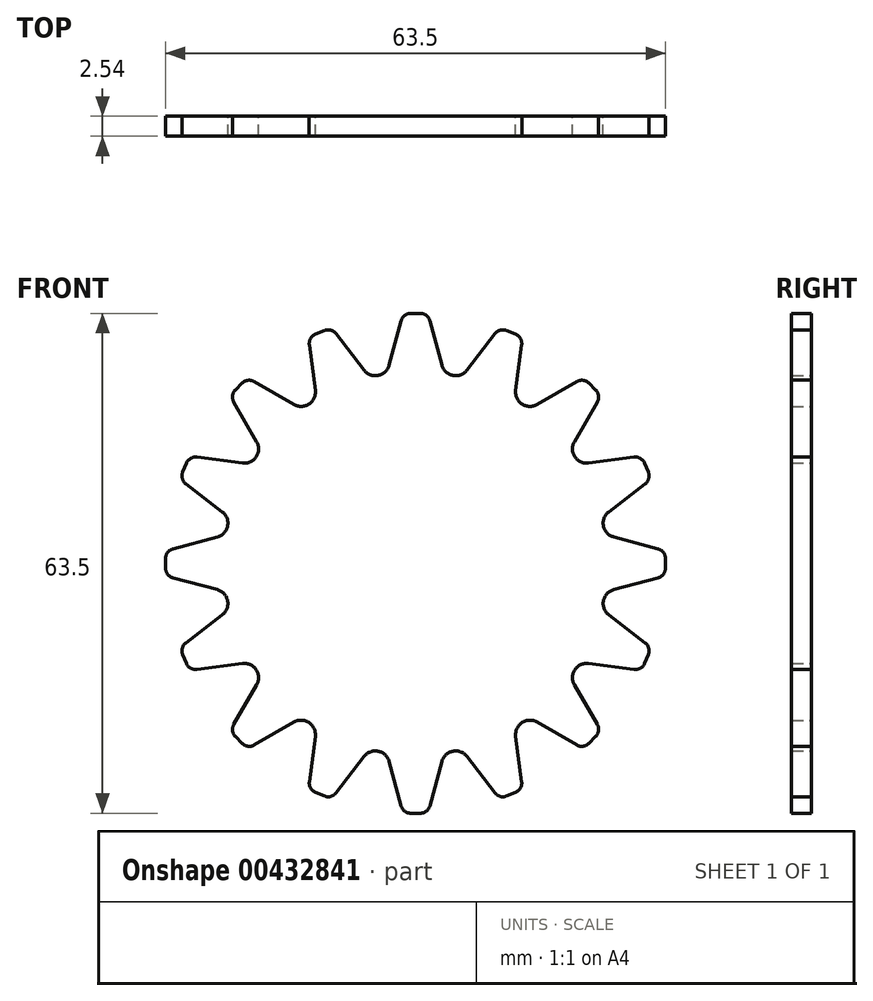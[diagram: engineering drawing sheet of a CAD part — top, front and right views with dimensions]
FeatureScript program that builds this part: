
annotation { "Feature Type Name" : "Feature", "Feature Type Description" : "" }
export const myFeature = defineFeature(function(context is Context, id is Id, definition is map)
    precondition{}
    {
        {
            var Q0;
            Q0=qCreatedBy(makeId("Front.planeOp"),FACE);
            var sketch = newSketch(context, id + "F0", { "sketchPlane" : qUnion([Q0])});
            skCircle(sketch, "E0", {"center": v(0, 0) * mm, "radius": 25.4 * mm, "construction": true});
            skLineSegment(sketch, "E1", {"start": v(0, 48.3) * mm, "end": v(0, -16.63) * mm, "construction": true});
            skPoint(sketch, "E2", {"position": v(0, 31.75) * mm});
            skLineSegment(sketch, "E3", {"start": v(1.59, 31.75) * mm, "end": v(-0.61, 31.75) * mm});
            skLineSegment(sketch, "E4", {"start": v(-1.84, 30.8) * mm, "end": v(-3.35, 25.18) * mm});
            skPoint(sketch, "E5.visualSharp", {"position": v(-1.59, 31.75) * mm});
            skArc(sketch, "E5.filletArc", {"start": v(-0.61, 31.75) * mm, "mid": v(-1.39, 31.49) * mm, "end": v(-1.84, 30.8) * mm});
            skLineSegment(sketch, "E6.MirrorCS", {"start": v(1.84, 30.8) * mm, "end": v(3.35, 25.18) * mm});
            skArc(sketch, "E7.MirrorCS", {"start": v(0.61, 31.75) * mm, "mid": v(1.39, 31.49) * mm, "end": v(1.84, 30.8) * mm});
            skArc(sketch, "E8", {"start": v(3.35, 25.18) * mm, "mid": v(4.75, 23.87) * mm, "end": v(6.54, 24.54) * mm});
            skLineSegment(sketch, "E9.1.0", {"start": v(-10.1, 29.17) * mm, "end": v(-6.54, 24.54) * mm});
            skPoint(sketch, "E9.1.1", {"position": v(-13.62, 28.73) * mm});
            skLineSegment(sketch, "E9.1.2", {"start": v(-13.49, 27.76) * mm, "end": v(-12.73, 21.98) * mm});
            skArc(sketch, "E9.1.3", {"start": v(-6.54, 24.54) * mm, "mid": v(-4.75, 23.87) * mm, "end": v(-3.35, 25.18) * mm});
            skPoint(sketch, "E9.1.4", {"position": v(-12.15, 29.33) * mm});
            skLineSegment(sketch, "E9.1.5", {"start": v(-10.68, 29.94) * mm, "end": v(-12.72, 29.1) * mm});
            skArc(sketch, "E9.1.6", {"start": v(-11.58, 29.57) * mm, "mid": v(-10.77, 29.62) * mm, "end": v(-10.1, 29.17) * mm});
            skArc(sketch, "E9.1.7", {"start": v(-12.72, 29.1) * mm, "mid": v(-13.33, 28.56) * mm, "end": v(-13.49, 27.76) * mm});
            skLineSegment(sketch, "E9.2.0", {"start": v(-20.48, 23.09) * mm, "end": v(-15.44, 20.17) * mm});
            skPoint(sketch, "E9.2.1", {"position": v(-23.57, 21.33) * mm});
            skLineSegment(sketch, "E9.2.2", {"start": v(-23.09, 20.48) * mm, "end": v(-20.17, 15.44) * mm});
            skArc(sketch, "E9.2.3", {"start": v(-15.44, 20.17) * mm, "mid": v(-13.52, 20.23) * mm, "end": v(-12.73, 21.98) * mm});
            skPoint(sketch, "E9.2.4", {"position": v(-22.45, 22.45) * mm});
            skLineSegment(sketch, "E9.2.5", {"start": v(-21.33, 23.57) * mm, "end": v(-22.88, 22.02) * mm});
            skArc(sketch, "E9.2.6", {"start": v(-22.02, 22.88) * mm, "mid": v(-21.28, 23.25) * mm, "end": v(-20.48, 23.09) * mm});
            skArc(sketch, "E9.2.7", {"start": v(-22.88, 22.02) * mm, "mid": v(-23.25, 21.28) * mm, "end": v(-23.09, 20.48) * mm});
            skLineSegment(sketch, "E9.3.0", {"start": v(-27.76, 13.49) * mm, "end": v(-21.98, 12.73) * mm});
            skPoint(sketch, "E9.3.1", {"position": v(-29.94, 10.68) * mm});
            skLineSegment(sketch, "E9.3.2", {"start": v(-29.17, 10.1) * mm, "end": v(-24.54, 6.54) * mm});
            skArc(sketch, "E9.3.3", {"start": v(-21.98, 12.73) * mm, "mid": v(-20.23, 13.52) * mm, "end": v(-20.17, 15.44) * mm});
            skPoint(sketch, "E9.3.4", {"position": v(-29.33, 12.15) * mm});
            skLineSegment(sketch, "E9.3.5", {"start": v(-28.73, 13.62) * mm, "end": v(-29.57, 11.58) * mm});
            skArc(sketch, "E9.3.6", {"start": v(-29.1, 12.72) * mm, "mid": v(-28.56, 13.33) * mm, "end": v(-27.76, 13.49) * mm});
            skArc(sketch, "E9.3.7", {"start": v(-29.57, 11.58) * mm, "mid": v(-29.62, 10.77) * mm, "end": v(-29.17, 10.1) * mm});
            skLineSegment(sketch, "E9.4.0", {"start": v(-30.8, 1.84) * mm, "end": v(-25.18, 3.35) * mm});
            skPoint(sketch, "E9.4.1", {"position": v(-31.75, -1.59) * mm});
            skLineSegment(sketch, "E9.4.2", {"start": v(-30.8, -1.84) * mm, "end": v(-25.18, -3.35) * mm});
            skArc(sketch, "E9.4.3", {"start": v(-25.18, 3.35) * mm, "mid": v(-23.87, 4.75) * mm, "end": v(-24.54, 6.54) * mm});
            skPoint(sketch, "E9.4.4", {"position": v(-31.75, 0) * mm});
            skLineSegment(sketch, "E9.4.5", {"start": v(-31.75, 1.59) * mm, "end": v(-31.75, -0.61) * mm});
            skArc(sketch, "E9.4.6", {"start": v(-31.75, 0.61) * mm, "mid": v(-31.49, 1.39) * mm, "end": v(-30.8, 1.84) * mm});
            skArc(sketch, "E9.4.7", {"start": v(-31.75, -0.61) * mm, "mid": v(-31.49, -1.39) * mm, "end": v(-30.8, -1.84) * mm});
            skLineSegment(sketch, "E9.5.0", {"start": v(-29.17, -10.1) * mm, "end": v(-24.54, -6.54) * mm});
            skPoint(sketch, "E9.5.1", {"position": v(-28.73, -13.62) * mm});
            skLineSegment(sketch, "E9.5.2", {"start": v(-27.76, -13.49) * mm, "end": v(-21.98, -12.73) * mm});
            skArc(sketch, "E9.5.3", {"start": v(-24.54, -6.54) * mm, "mid": v(-23.87, -4.75) * mm, "end": v(-25.18, -3.35) * mm});
            skPoint(sketch, "E9.5.4", {"position": v(-29.33, -12.15) * mm});
            skLineSegment(sketch, "E9.5.5", {"start": v(-29.94, -10.68) * mm, "end": v(-29.1, -12.72) * mm});
            skArc(sketch, "E9.5.6", {"start": v(-29.57, -11.58) * mm, "mid": v(-29.62, -10.77) * mm, "end": v(-29.17, -10.1) * mm});
            skArc(sketch, "E9.5.7", {"start": v(-29.1, -12.72) * mm, "mid": v(-28.56, -13.33) * mm, "end": v(-27.76, -13.49) * mm});
            skLineSegment(sketch, "E9.6.0", {"start": v(-23.09, -20.48) * mm, "end": v(-20.17, -15.44) * mm});
            skPoint(sketch, "E9.6.1", {"position": v(-21.33, -23.57) * mm});
            skLineSegment(sketch, "E9.6.2", {"start": v(-20.48, -23.09) * mm, "end": v(-15.44, -20.17) * mm});
            skArc(sketch, "E9.6.3", {"start": v(-20.17, -15.44) * mm, "mid": v(-20.23, -13.52) * mm, "end": v(-21.98, -12.73) * mm});
            skPoint(sketch, "E9.6.4", {"position": v(-22.45, -22.45) * mm});
            skLineSegment(sketch, "E9.6.5", {"start": v(-23.57, -21.33) * mm, "end": v(-22.02, -22.88) * mm});
            skArc(sketch, "E9.6.6", {"start": v(-22.88, -22.02) * mm, "mid": v(-23.25, -21.28) * mm, "end": v(-23.09, -20.48) * mm});
            skArc(sketch, "E9.6.7", {"start": v(-22.02, -22.88) * mm, "mid": v(-21.28, -23.25) * mm, "end": v(-20.48, -23.09) * mm});
            skLineSegment(sketch, "E9.7.0", {"start": v(-13.49, -27.76) * mm, "end": v(-12.73, -21.98) * mm});
            skPoint(sketch, "E9.7.1", {"position": v(-10.68, -29.94) * mm});
            skLineSegment(sketch, "E9.7.2", {"start": v(-10.1, -29.17) * mm, "end": v(-6.54, -24.54) * mm});
            skArc(sketch, "E9.7.3", {"start": v(-12.73, -21.98) * mm, "mid": v(-13.52, -20.23) * mm, "end": v(-15.44, -20.17) * mm});
            skPoint(sketch, "E9.7.4", {"position": v(-12.15, -29.33) * mm});
            skLineSegment(sketch, "E9.7.5", {"start": v(-13.62, -28.73) * mm, "end": v(-11.58, -29.57) * mm});
            skArc(sketch, "E9.7.6", {"start": v(-12.72, -29.1) * mm, "mid": v(-13.33, -28.56) * mm, "end": v(-13.49, -27.76) * mm});
            skArc(sketch, "E9.7.7", {"start": v(-11.58, -29.57) * mm, "mid": v(-10.77, -29.62) * mm, "end": v(-10.1, -29.17) * mm});
            skLineSegment(sketch, "E9.8.0", {"start": v(-1.84, -30.8) * mm, "end": v(-3.35, -25.18) * mm});
            skPoint(sketch, "E9.8.1", {"position": v(1.59, -31.75) * mm});
            skLineSegment(sketch, "E9.8.2", {"start": v(1.84, -30.8) * mm, "end": v(3.35, -25.18) * mm});
            skArc(sketch, "E9.8.3", {"start": v(-3.35, -25.18) * mm, "mid": v(-4.75, -23.87) * mm, "end": v(-6.54, -24.54) * mm});
            skPoint(sketch, "E9.8.4", {"position": v(0, -31.75) * mm});
            skLineSegment(sketch, "E9.8.5", {"start": v(-1.59, -31.75) * mm, "end": v(0.61, -31.75) * mm});
            skArc(sketch, "E9.8.6", {"start": v(-0.61, -31.75) * mm, "mid": v(-1.39, -31.49) * mm, "end": v(-1.84, -30.8) * mm});
            skArc(sketch, "E9.8.7", {"start": v(0.61, -31.75) * mm, "mid": v(1.39, -31.49) * mm, "end": v(1.84, -30.8) * mm});
            skLineSegment(sketch, "E9.9.0", {"start": v(10.1, -29.17) * mm, "end": v(6.54, -24.54) * mm});
            skPoint(sketch, "E9.9.1", {"position": v(13.62, -28.73) * mm});
            skLineSegment(sketch, "E9.9.2", {"start": v(13.49, -27.76) * mm, "end": v(12.73, -21.98) * mm});
            skArc(sketch, "E9.9.3", {"start": v(6.54, -24.54) * mm, "mid": v(4.75, -23.87) * mm, "end": v(3.35, -25.18) * mm});
            skPoint(sketch, "E9.9.4", {"position": v(12.15, -29.33) * mm});
            skLineSegment(sketch, "E9.9.5", {"start": v(10.68, -29.94) * mm, "end": v(12.72, -29.1) * mm});
            skArc(sketch, "E9.9.6", {"start": v(11.58, -29.57) * mm, "mid": v(10.77, -29.62) * mm, "end": v(10.1, -29.17) * mm});
            skArc(sketch, "E9.9.7", {"start": v(12.72, -29.1) * mm, "mid": v(13.33, -28.56) * mm, "end": v(13.49, -27.76) * mm});
            skLineSegment(sketch, "E9.10.0", {"start": v(20.48, -23.09) * mm, "end": v(15.44, -20.17) * mm});
            skPoint(sketch, "E9.10.1", {"position": v(23.57, -21.33) * mm});
            skLineSegment(sketch, "E9.10.2", {"start": v(23.09, -20.48) * mm, "end": v(20.17, -15.44) * mm});
            skArc(sketch, "E9.10.3", {"start": v(15.44, -20.17) * mm, "mid": v(13.52, -20.23) * mm, "end": v(12.73, -21.98) * mm});
            skPoint(sketch, "E9.10.4", {"position": v(22.45, -22.45) * mm});
            skLineSegment(sketch, "E9.10.5", {"start": v(21.33, -23.57) * mm, "end": v(22.88, -22.02) * mm});
            skArc(sketch, "E9.10.6", {"start": v(22.02, -22.88) * mm, "mid": v(21.28, -23.25) * mm, "end": v(20.48, -23.09) * mm});
            skArc(sketch, "E9.10.7", {"start": v(22.88, -22.02) * mm, "mid": v(23.25, -21.28) * mm, "end": v(23.09, -20.48) * mm});
            skLineSegment(sketch, "E9.11.0", {"start": v(27.76, -13.49) * mm, "end": v(21.98, -12.73) * mm});
            skPoint(sketch, "E9.11.1", {"position": v(29.94, -10.68) * mm});
            skLineSegment(sketch, "E9.11.2", {"start": v(29.17, -10.1) * mm, "end": v(24.54, -6.54) * mm});
            skArc(sketch, "E9.11.3", {"start": v(21.98, -12.73) * mm, "mid": v(20.23, -13.52) * mm, "end": v(20.17, -15.44) * mm});
            skPoint(sketch, "E9.11.4", {"position": v(29.33, -12.15) * mm});
            skLineSegment(sketch, "E9.11.5", {"start": v(28.73, -13.62) * mm, "end": v(29.57, -11.58) * mm});
            skArc(sketch, "E9.11.6", {"start": v(29.1, -12.72) * mm, "mid": v(28.56, -13.33) * mm, "end": v(27.76, -13.49) * mm});
            skArc(sketch, "E9.11.7", {"start": v(29.57, -11.58) * mm, "mid": v(29.62, -10.77) * mm, "end": v(29.17, -10.1) * mm});
            skLineSegment(sketch, "E9.12.0", {"start": v(30.8, -1.84) * mm, "end": v(25.18, -3.35) * mm});
            skPoint(sketch, "E9.12.1", {"position": v(31.75, 1.59) * mm});
            skLineSegment(sketch, "E9.12.2", {"start": v(30.8, 1.84) * mm, "end": v(25.18, 3.35) * mm});
            skArc(sketch, "E9.12.3", {"start": v(25.18, -3.35) * mm, "mid": v(23.87, -4.75) * mm, "end": v(24.54, -6.54) * mm});
            skPoint(sketch, "E9.12.4", {"position": v(31.75, 0) * mm});
            skLineSegment(sketch, "E9.12.5", {"start": v(31.75, -1.59) * mm, "end": v(31.75, 0.61) * mm});
            skArc(sketch, "E9.12.6", {"start": v(31.75, -0.61) * mm, "mid": v(31.49, -1.39) * mm, "end": v(30.8, -1.84) * mm});
            skArc(sketch, "E9.12.7", {"start": v(31.75, 0.61) * mm, "mid": v(31.49, 1.39) * mm, "end": v(30.8, 1.84) * mm});
            skLineSegment(sketch, "E9.13.0", {"start": v(29.17, 10.1) * mm, "end": v(24.54, 6.54) * mm});
            skPoint(sketch, "E9.13.1", {"position": v(28.73, 13.62) * mm});
            skLineSegment(sketch, "E9.13.2", {"start": v(27.76, 13.49) * mm, "end": v(21.98, 12.73) * mm});
            skArc(sketch, "E9.13.3", {"start": v(24.54, 6.54) * mm, "mid": v(23.87, 4.75) * mm, "end": v(25.18, 3.35) * mm});
            skPoint(sketch, "E9.13.4", {"position": v(29.33, 12.15) * mm});
            skLineSegment(sketch, "E9.13.5", {"start": v(29.94, 10.68) * mm, "end": v(29.1, 12.72) * mm});
            skArc(sketch, "E9.13.6", {"start": v(29.57, 11.58) * mm, "mid": v(29.62, 10.77) * mm, "end": v(29.17, 10.1) * mm});
            skArc(sketch, "E9.13.7", {"start": v(29.1, 12.72) * mm, "mid": v(28.56, 13.33) * mm, "end": v(27.76, 13.49) * mm});
            skLineSegment(sketch, "E9.14.0", {"start": v(23.09, 20.48) * mm, "end": v(20.17, 15.44) * mm});
            skPoint(sketch, "E9.14.1", {"position": v(21.33, 23.57) * mm});
            skLineSegment(sketch, "E9.14.2", {"start": v(20.48, 23.09) * mm, "end": v(15.44, 20.17) * mm});
            skArc(sketch, "E9.14.3", {"start": v(20.17, 15.44) * mm, "mid": v(20.23, 13.52) * mm, "end": v(21.98, 12.73) * mm});
            skPoint(sketch, "E9.14.4", {"position": v(22.45, 22.45) * mm});
            skLineSegment(sketch, "E9.14.5", {"start": v(23.57, 21.33) * mm, "end": v(22.02, 22.88) * mm});
            skArc(sketch, "E9.14.6", {"start": v(22.88, 22.02) * mm, "mid": v(23.25, 21.28) * mm, "end": v(23.09, 20.48) * mm});
            skArc(sketch, "E9.14.7", {"start": v(22.02, 22.88) * mm, "mid": v(21.28, 23.25) * mm, "end": v(20.48, 23.09) * mm});
            skLineSegment(sketch, "E9.15.0", {"start": v(13.49, 27.76) * mm, "end": v(12.73, 21.98) * mm});
            skPoint(sketch, "E9.15.1", {"position": v(10.68, 29.94) * mm});
            skLineSegment(sketch, "E9.15.2", {"start": v(10.1, 29.17) * mm, "end": v(6.54, 24.54) * mm});
            skArc(sketch, "E9.15.3", {"start": v(12.73, 21.98) * mm, "mid": v(13.52, 20.23) * mm, "end": v(15.44, 20.17) * mm});
            skPoint(sketch, "E9.15.4", {"position": v(12.15, 29.33) * mm});
            skLineSegment(sketch, "E9.15.5", {"start": v(13.62, 28.73) * mm, "end": v(11.58, 29.57) * mm});
            skArc(sketch, "E9.15.6", {"start": v(12.72, 29.1) * mm, "mid": v(13.33, 28.56) * mm, "end": v(13.49, 27.76) * mm});
            skArc(sketch, "E9.15.7", {"start": v(11.58, 29.57) * mm, "mid": v(10.77, 29.62) * mm, "end": v(10.1, 29.17) * mm});
            skSolve(sketch);
        }
        {
            var Q0;
            Q0=makeQuery(id+"F0.imprint","IMPRINT",FACE,{"disambiguationData":[TD([[makeQuery(id+"F0.imprint","IMPRINT",EDGE,{"derivedFrom":sQuery(id+"F0.wireOp",EDGE,"E4")}),1.0]])]});
            extrude(context, id + "F1", {"entities" : qUnion([Q0]), "depth" : 2.54 * mm});
        }
    });
